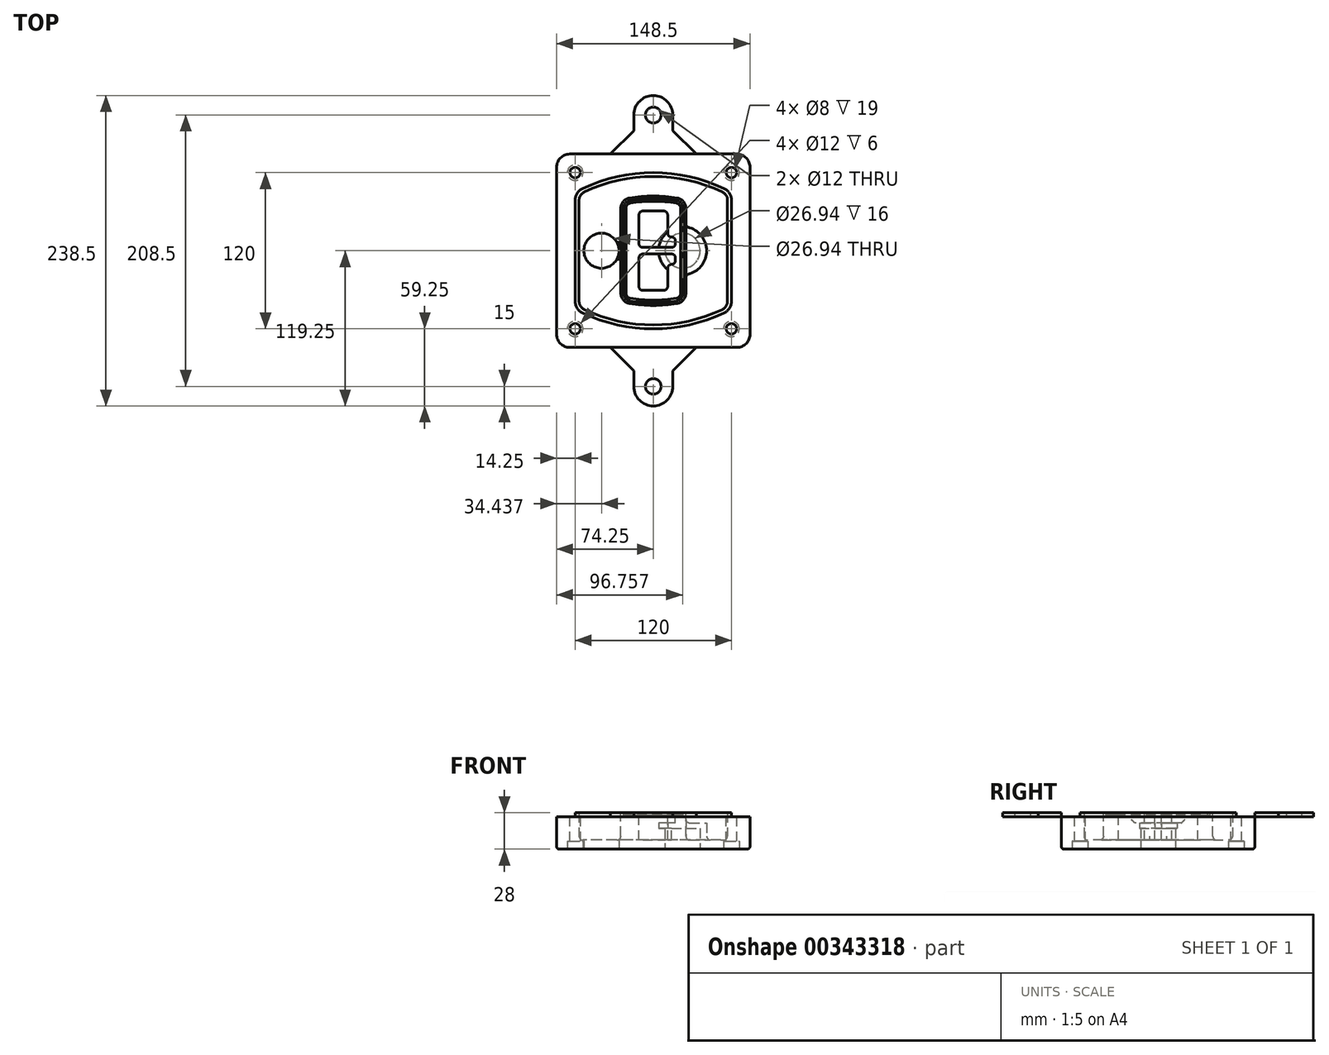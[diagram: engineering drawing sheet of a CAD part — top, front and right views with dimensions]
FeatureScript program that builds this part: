
annotation { "Feature Type Name" : "Feature", "Feature Type Description" : "" }
export const myFeature = defineFeature(function(context is Context, id is Id, definition is map)
    precondition{}
    {
        {
            var Q0;
            Q0=qCreatedBy(makeId("Top.planeOp"),FACE);
            var sketch = newSketch(context, id + "F0", { "sketchPlane" : qUnion([Q0])});
            skPoint(sketch, "E0.rect.middle", {"position": v(0, 0) * mm});
            skLineSegment(sketch, "E1.bottom", {"start": v(-64.25, -74.25) * mm, "end": v(64.25, -74.25) * mm});
            skLineSegment(sketch, "E1.top", {"start": v(-64.25, 74.25) * mm, "end": v(64.25, 74.25) * mm});
            skLineSegment(sketch, "E1.left", {"start": v(-74.25, -64.25) * mm, "end": v(-74.25, 64.25) * mm});
            skLineSegment(sketch, "E1.right", {"start": v(74.25, -64.25) * mm, "end": v(74.25, 64.25) * mm});
            skLineSegment(sketch, "E2", {"start": v(-74.25, 74.25) * mm, "end": v(74.25, -74.25) * mm, "construction": true});
            skLineSegment(sketch, "E3", {"start": v(74.25, 74.25) * mm, "end": v(-74.25, -74.25) * mm, "construction": true});
            skCircle(sketch, "E4", {"center": v(-60, 60) * mm, "radius": 4 * mm});
            skCircle(sketch, "E5", {"center": v(60, 60) * mm, "radius": 4 * mm});
            skCircle(sketch, "E6", {"center": v(60, -60) * mm, "radius": 4 * mm});
            skCircle(sketch, "E7", {"center": v(-60, -60) * mm, "radius": 4 * mm});
            skLineSegment(sketch, "E8", {"start": v(-60, 60) * mm, "end": v(60, 60) * mm, "construction": true});
            skLineSegment(sketch, "E9", {"start": v(60, 60) * mm, "end": v(60, -60) * mm, "construction": true});
            skLineSegment(sketch, "E10", {"start": v(60, -60) * mm, "end": v(-60, -60) * mm, "construction": true});
            skLineSegment(sketch, "E11", {"start": v(-60, -60) * mm, "end": v(-60, 60) * mm, "construction": true});
            skLineSegment(sketch, "E12", {"start": v(-60, 38.83) * mm, "end": v(-60, -38.83) * mm});
            skLineSegment(sketch, "E13", {"start": v(60, 38.83) * mm, "end": v(60, -38.83) * mm});
            skArc(sketch, "E14", {"start": v(54.26, 47.88) * mm, "mid": v(0, 60) * mm, "end": v(-54.26, 47.88) * mm});
            skArc(sketch, "E15", {"start": v(-54.26, -47.88) * mm, "mid": v(0, -60) * mm, "end": v(54.26, -47.88) * mm});
            skLineSegment(sketch, "E16", {"start": v(-60, 0) * mm, "end": v(60, 0) * mm, "construction": true});
            skPoint(sketch, "E17.visualSharp", {"position": v(-60, -45) * mm});
            skArc(sketch, "E17.filletArc", {"start": v(-60, -38.83) * mm, "mid": v(-58.44, -44.2) * mm, "end": v(-54.26, -47.88) * mm});
            skPoint(sketch, "E18.visualSharp", {"position": v(-60, 45) * mm});
            skArc(sketch, "E18.filletArc", {"start": v(-54.26, 47.88) * mm, "mid": v(-58.44, 44.2) * mm, "end": v(-60, 38.83) * mm});
            skPoint(sketch, "E19.visualSharp", {"position": v(60, 45) * mm});
            skArc(sketch, "E19.filletArc", {"start": v(60, 38.83) * mm, "mid": v(58.44, 44.2) * mm, "end": v(54.26, 47.88) * mm});
            skPoint(sketch, "E20.visualSharp", {"position": v(60, -45) * mm});
            skArc(sketch, "E20.filletArc", {"start": v(54.26, -47.88) * mm, "mid": v(58.44, -44.2) * mm, "end": v(60, -38.83) * mm});
            skPoint(sketch, "E21.visualSharp", {"position": v(-74.25, 74.25) * mm});
            skArc(sketch, "E21.filletArc", {"start": v(-64.25, 74.25) * mm, "mid": v(-71.32, 71.32) * mm, "end": v(-74.25, 64.25) * mm});
            skPoint(sketch, "E22.visualSharp", {"position": v(74.25, 74.25) * mm});
            skArc(sketch, "E22.filletArc", {"start": v(74.25, 64.25) * mm, "mid": v(71.32, 71.32) * mm, "end": v(64.25, 74.25) * mm});
            skPoint(sketch, "E23.visualSharp", {"position": v(74.25, -74.25) * mm});
            skArc(sketch, "E23.filletArc", {"start": v(64.25, -74.25) * mm, "mid": v(71.32, -71.32) * mm, "end": v(74.25, -64.25) * mm});
            skPoint(sketch, "E24.visualSharp", {"position": v(-74.25, -74.25) * mm});
            skArc(sketch, "E24.filletArc", {"start": v(-74.25, -64.25) * mm, "mid": v(-71.32, -71.32) * mm, "end": v(-64.25, -74.25) * mm});
            skArc(sketch, "E25.0", {"start": v(57, 38.83) * mm, "mid": v(55.9, 42.58) * mm, "end": v(52.98, 45.17) * mm});
            skLineSegment(sketch, "E25.1", {"start": v(57, 38.83) * mm, "end": v(57, -38.83) * mm});
            skArc(sketch, "E25.2", {"start": v(52.98, -45.17) * mm, "mid": v(55.9, -42.58) * mm, "end": v(57, -38.83) * mm});
            skArc(sketch, "E25.3", {"start": v(-52.98, -45.17) * mm, "mid": v(0, -57) * mm, "end": v(52.98, -45.17) * mm});
            skArc(sketch, "E25.4", {"start": v(-57, -38.83) * mm, "mid": v(-55.9, -42.58) * mm, "end": v(-52.98, -45.17) * mm});
            skArc(sketch, "E25.5", {"start": v(52.98, 45.17) * mm, "mid": v(0, 57) * mm, "end": v(-52.98, 45.17) * mm});
            skLineSegment(sketch, "E25.6", {"start": v(-57, 38.83) * mm, "end": v(-57, -38.83) * mm});
            skArc(sketch, "E25.7", {"start": v(-52.98, 45.17) * mm, "mid": v(-55.9, 42.58) * mm, "end": v(-57, 38.83) * mm});
            skArc(sketch, "E26.0", {"start": v(-55.96, 51.5) * mm, "mid": v(-61.82, 46.33) * mm, "end": v(-64, 38.83) * mm});
            skArc(sketch, "E26.1", {"start": v(55.96, 51.5) * mm, "mid": v(0, 64) * mm, "end": v(-55.96, 51.5) * mm});
            skArc(sketch, "E26.2", {"start": v(64, 38.83) * mm, "mid": v(61.82, 46.33) * mm, "end": v(55.96, 51.5) * mm});
            skLineSegment(sketch, "E26.3", {"start": v(64, 38.83) * mm, "end": v(64, -38.83) * mm});
            skArc(sketch, "E26.4", {"start": v(55.96, -51.5) * mm, "mid": v(61.82, -46.33) * mm, "end": v(64, -38.83) * mm});
            skLineSegment(sketch, "E26.5", {"start": v(-64, 38.83) * mm, "end": v(-64, -38.83) * mm});
            skArc(sketch, "E26.6", {"start": v(-55.96, -51.5) * mm, "mid": v(0, -64) * mm, "end": v(55.96, -51.5) * mm});
            skArc(sketch, "E26.7", {"start": v(-64, -38.83) * mm, "mid": v(-61.82, -46.33) * mm, "end": v(-55.96, -51.5) * mm});
            skSolve(sketch);
        }
        {
            var Q0;
            Q0=makeQuery(id+"F0.imprint","IMPRINT",FACE,{"disambiguationData":[TD([[makeQuery(id+"F0.imprint","IMPRINT",EDGE,{"derivedFrom":sQuery(id+"F0.wireOp",EDGE,"E1.bottom")}),1.0]])]});
            var Q1;
            Q1=makeQuery(id+"F0.imprint","IMPRINT",FACE,{"disambiguationData":[TD([[makeQuery(id+"F0.imprint","IMPRINT",EDGE,{"derivedFrom":sQuery(id+"F0.wireOp",EDGE,"E12")}),1.0]])]});
            var Q2;
            Q2=makeQuery(id+"F0.imprint","IMPRINT",FACE,{"disambiguationData":[TD([[makeQuery(id+"F0.imprint","IMPRINT",EDGE,{"derivedFrom":sQuery(id+"F0.wireOp",EDGE,"E25.0")}),1.0]])]});
            var Q3;
            Q3=makeQuery(id+"F0.imprint","IMPRINT",FACE,{"disambiguationData":[TD([[makeQuery(id+"F0.imprint","IMPRINT",EDGE,{"derivedFrom":sQuery(id+"F0.wireOp",EDGE,"E12")}),-1.0]])]});
            extrude(context, id + "F1", {"entities" : qUnion([Q0, Q1, Q2, Q3]), "oppositeDirection" : true, "depth" : 25 * mm});
        }
        {
            var Q0;
            Q0=makeQuery(id+"F0.imprint","IMPRINT",FACE,{"disambiguationData":[TD([[makeQuery(id+"F0.imprint","IMPRINT",EDGE,{"derivedFrom":sQuery(id+"F0.wireOp",EDGE,"E12")}),1.0]])]});
            extrude(context, id + "F2", {"entities" : qUnion([Q0]), "operationType" : NewBodyOperationType.ADD, "depth" : 3 * mm});
        }
        {
            var Q0;
            Q0=makeQuery(id+"F0.imprint","IMPRINT",FACE,{"disambiguationData":[TD([[makeQuery(id+"F0.imprint","IMPRINT",EDGE,{"derivedFrom":sQuery(id+"F0.wireOp",EDGE,"E25.0")}),1.0]])]});
            extrude(context, id + "F3", {"entities" : qUnion([Q0]), "operationType" : NewBodyOperationType.REMOVE, "oppositeDirection" : true, "depth" : 18 * mm});
        }
        {
            var Q0;
            Q0=makeQuery(id+"F2.opExtrude","CAP_FACE",FACE,{"disambiguationData":[OSD([sQuery(id+"F0.wireOp",EDGE,"E12"),sQuery(id+"F0.wireOp",EDGE,"E13"),sQuery(id+"F0.wireOp",EDGE,"E14"),sQuery(id+"F0.wireOp",EDGE,"E15"),sQuery(id+"F0.wireOp",EDGE,"E17.filletArc"),sQuery(id+"F0.wireOp",EDGE,"E18.filletArc"),sQuery(id+"F0.wireOp",EDGE,"E19.filletArc"),sQuery(id+"F0.wireOp",EDGE,"E20.filletArc"),sQuery(id+"F0.wireOp",EDGE,"E25.0"),sQuery(id+"F0.wireOp",EDGE,"E25.1"),sQuery(id+"F0.wireOp",EDGE,"E25.2"),sQuery(id+"F0.wireOp",EDGE,"E25.3"),sQuery(id+"F0.wireOp",EDGE,"E25.4"),sQuery(id+"F0.wireOp",EDGE,"E25.5"),sQuery(id+"F0.wireOp",EDGE,"E25.6"),sQuery(id+"F0.wireOp",EDGE,"E25.7")])],"isStart":false});
            var sketch = newSketch(context, id + "F4", { "sketchPlane" : qUnion([Q0])});
            skArc(sketch, "E27.0", {"start": v(-18.34, -40.45) * mm, "mid": v(0, -42) * mm, "end": v(18.34, -40.45) * mm});
            skArc(sketch, "E28.0", {"start": v(18.34, 40.45) * mm, "mid": v(0, 42) * mm, "end": v(-18.34, 40.45) * mm});
            skLineSegment(sketch, "E29", {"start": v(-25, 32.57) * mm, "end": v(-25, -32.57) * mm});
            skLineSegment(sketch, "E30", {"start": v(25, 32.57) * mm, "end": v(25, -32.57) * mm});
            skLineSegment(sketch, "E31", {"start": v(-25, 39.1) * mm, "end": v(25, 39.1) * mm, "construction": true});
            skLineSegment(sketch, "E32", {"start": v(-25, -39.1) * mm, "end": v(25, -39.1) * mm, "construction": true});
            skPoint(sketch, "E33.visualSharp", {"position": v(-25, 39.1) * mm});
            skArc(sketch, "E33.filletArc", {"start": v(-18.34, 40.45) * mm, "mid": v(-23.11, 37.73) * mm, "end": v(-25, 32.57) * mm});
            skPoint(sketch, "E34.visualSharp", {"position": v(25, 39.1) * mm});
            skArc(sketch, "E34.filletArc", {"start": v(25, 32.57) * mm, "mid": v(23.11, 37.73) * mm, "end": v(18.34, 40.45) * mm});
            skPoint(sketch, "E35.visualSharp", {"position": v(25, -39.1) * mm});
            skArc(sketch, "E35.filletArc", {"start": v(18.34, -40.45) * mm, "mid": v(23.11, -37.73) * mm, "end": v(25, -32.57) * mm});
            skPoint(sketch, "E36.visualSharp", {"position": v(-25, -39.1) * mm});
            skArc(sketch, "E36.filletArc", {"start": v(-25, -32.57) * mm, "mid": v(-23.11, -37.73) * mm, "end": v(-18.34, -40.45) * mm});
            skArc(sketch, "E37.0", {"start": v(52.98, 45.17) * mm, "mid": v(0, 57) * mm, "end": v(-52.98, 45.17) * mm});
            skArc(sketch, "E37.1", {"start": v(-52.98, 45.17) * mm, "mid": v(-55.9, 42.58) * mm, "end": v(-57, 38.83) * mm});
            skLineSegment(sketch, "E37.2", {"start": v(-57, 38.83) * mm, "end": v(-57, -38.83) * mm});
            skArc(sketch, "E37.3", {"start": v(-57, -38.83) * mm, "mid": v(-55.9, -42.58) * mm, "end": v(-52.98, -45.17) * mm});
            skArc(sketch, "E37.4", {"start": v(-52.98, -45.17) * mm, "mid": v(0, -57) * mm, "end": v(52.98, -45.17) * mm});
            skArc(sketch, "E37.5", {"start": v(52.98, -45.17) * mm, "mid": v(55.9, -42.58) * mm, "end": v(57, -38.83) * mm});
            skLineSegment(sketch, "E37.6", {"start": v(57, 38.83) * mm, "end": v(57, -38.83) * mm});
            skArc(sketch, "E37.7", {"start": v(57, 38.83) * mm, "mid": v(55.9, 42.58) * mm, "end": v(52.98, 45.17) * mm});
            skLineSegment(sketch, "E38.0", {"start": v(23, 32.57) * mm, "end": v(23, -32.57) * mm});
            skArc(sketch, "E38.1", {"start": v(18, -38.48) * mm, "mid": v(21.58, -36.44) * mm, "end": v(23, -32.57) * mm});
            skArc(sketch, "E38.2", {"start": v(-18, -38.48) * mm, "mid": v(0, -40) * mm, "end": v(18, -38.48) * mm});
            skArc(sketch, "E38.3", {"start": v(-23, -32.57) * mm, "mid": v(-21.58, -36.44) * mm, "end": v(-18, -38.48) * mm});
            skLineSegment(sketch, "E38.4", {"start": v(-23, 32.57) * mm, "end": v(-23, -32.57) * mm});
            skArc(sketch, "E38.5", {"start": v(23, 32.57) * mm, "mid": v(21.58, 36.44) * mm, "end": v(18, 38.48) * mm});
            skArc(sketch, "E38.6", {"start": v(-18, 38.48) * mm, "mid": v(-21.58, 36.44) * mm, "end": v(-23, 32.57) * mm});
            skArc(sketch, "E38.7", {"start": v(18, 38.48) * mm, "mid": v(0, 40) * mm, "end": v(-18, 38.48) * mm});
            skArc(sketch, "E39.0", {"start": v(21, 32.57) * mm, "mid": v(20.06, 35.15) * mm, "end": v(17.67, 36.5) * mm});
            skLineSegment(sketch, "E39.1", {"start": v(21, 32.57) * mm, "end": v(21, -32.57) * mm});
            skArc(sketch, "E39.2", {"start": v(17.67, -36.5) * mm, "mid": v(20.06, -35.15) * mm, "end": v(21, -32.57) * mm});
            skArc(sketch, "E39.3", {"start": v(-17.67, -36.5) * mm, "mid": v(0, -38) * mm, "end": v(17.67, -36.5) * mm});
            skArc(sketch, "E39.4", {"start": v(-21, -32.57) * mm, "mid": v(-20.06, -35.15) * mm, "end": v(-17.67, -36.5) * mm});
            skArc(sketch, "E39.5", {"start": v(17.67, 36.5) * mm, "mid": v(0, 38) * mm, "end": v(-17.67, 36.5) * mm});
            skLineSegment(sketch, "E39.6", {"start": v(-21, 32.57) * mm, "end": v(-21, -32.57) * mm});
            skArc(sketch, "E39.7", {"start": v(-17.67, 36.5) * mm, "mid": v(-20.06, 35.15) * mm, "end": v(-21, 32.57) * mm});
            skLineSegment(sketch, "E40", {"start": v(-25, 0) * mm, "end": v(25, 0) * mm, "construction": true});
            skLineSegment(sketch, "E41", {"start": v(-11, 5.5) * mm, "end": v(-11, 27.5) * mm});
            skLineSegment(sketch, "E42", {"start": v(-8, 30.5) * mm, "end": v(8, 30.5) * mm});
            skLineSegment(sketch, "E43", {"start": v(11, 27.5) * mm, "end": v(11, 13.5) * mm});
            skLineSegment(sketch, "E44", {"start": v(14, 10.5) * mm, "end": v(14, 10.5) * mm});
            skLineSegment(sketch, "E45", {"start": v(17, 7.5) * mm, "end": v(17, 5.5) * mm});
            skLineSegment(sketch, "E46", {"start": v(14, 2.5) * mm, "end": v(-8, 2.5) * mm});
            skPoint(sketch, "E47.visualSharp", {"position": v(-11, 30.5) * mm});
            skArc(sketch, "E47.filletArc", {"start": v(-8, 30.5) * mm, "mid": v(-10.12, 29.62) * mm, "end": v(-11, 27.5) * mm});
            skPoint(sketch, "E48.visualSharp", {"position": v(11, 30.5) * mm});
            skArc(sketch, "E48.filletArc", {"start": v(11, 27.5) * mm, "mid": v(10.12, 29.62) * mm, "end": v(8, 30.5) * mm});
            skPoint(sketch, "E49.visualSharp", {"position": v(11, 10.5) * mm});
            skArc(sketch, "E49.filletArc", {"start": v(11, 13.5) * mm, "mid": v(11.88, 11.38) * mm, "end": v(14, 10.5) * mm});
            skPoint(sketch, "E50.visualSharp", {"position": v(17, 10.5) * mm});
            skArc(sketch, "E50.filletArc", {"start": v(17, 7.5) * mm, "mid": v(16.12, 9.62) * mm, "end": v(14, 10.5) * mm});
            skPoint(sketch, "E51.visualSharp", {"position": v(17, 2.5) * mm});
            skArc(sketch, "E51.filletArc", {"start": v(14, 2.5) * mm, "mid": v(16.12, 3.38) * mm, "end": v(17, 5.5) * mm});
            skPoint(sketch, "E52.visualSharp", {"position": v(-11, 2.5) * mm});
            skArc(sketch, "E52.filletArc", {"start": v(-11, 5.5) * mm, "mid": v(-10.12, 3.38) * mm, "end": v(-8, 2.5) * mm});
            skLineSegment(sketch, "E53.0.MirrorCS", {"start": v(14, -2.5) * mm, "end": v(-8, -2.5) * mm});
            skArc(sketch, "E54.0.MirrorCS", {"start": v(-11, -5.5) * mm, "mid": v(-10.12, -3.38) * mm, "end": v(-8, -2.5) * mm});
            skLineSegment(sketch, "E55.0.MirrorCS", {"start": v(-11, -5.5) * mm, "end": v(-11, -27.5) * mm});
            skArc(sketch, "E56.0.MirrorCS", {"start": v(-8, -30.5) * mm, "mid": v(-10.12, -29.62) * mm, "end": v(-11, -27.5) * mm});
            skLineSegment(sketch, "E57.0.MirrorCS", {"start": v(-8, -30.5) * mm, "end": v(8, -30.5) * mm});
            skArc(sketch, "E58.0.MirrorCS", {"start": v(11, -27.5) * mm, "mid": v(10.12, -29.62) * mm, "end": v(8, -30.5) * mm});
            skLineSegment(sketch, "E59.0.MirrorCS", {"start": v(11, -27.5) * mm, "end": v(11, -13.5) * mm});
            skArc(sketch, "E60.0.MirrorCS", {"start": v(11, -13.5) * mm, "mid": v(11.88, -11.38) * mm, "end": v(14, -10.5) * mm});
            skArc(sketch, "E61.0.MirrorCS", {"start": v(17, -7.5) * mm, "mid": v(16.12, -9.62) * mm, "end": v(14, -10.5) * mm});
            skLineSegment(sketch, "E62.0.MirrorCS", {"start": v(17, -7.5) * mm, "end": v(17, -5.5) * mm});
            skArc(sketch, "E63.0.MirrorCS", {"start": v(14, -2.5) * mm, "mid": v(16.12, -3.38) * mm, "end": v(17, -5.5) * mm});
            skSolve(sketch);
        }
        {
            var Q0;
            Q0=makeQuery(id+"F4.imprint","IMPRINT",FACE,{"disambiguationData":[TD([[makeQuery(id+"F4.imprint","IMPRINT",EDGE,{"derivedFrom":sQuery(id+"F4.wireOp",EDGE,"E27.0")}),1.0]])]});
            var Q1;
            Q1=makeQuery(id+"F4.imprint","IMPRINT",FACE,{"disambiguationData":[TD([[makeQuery(id+"F4.imprint","IMPRINT",EDGE,{"derivedFrom":sQuery(id+"F4.wireOp",EDGE,"E38.0")}),-1.0]])]});
            var Q2;
            Q2=makeQuery(id+"F4.imprint","IMPRINT",FACE,{"disambiguationData":[TD([[makeQuery(id+"F4.imprint","IMPRINT",EDGE,{"derivedFrom":sQuery(id+"F4.wireOp",EDGE,"E39.0")}),1.0]])]});
            extrude(context, id + "F5", {"entities" : qUnion([Q0, Q1, Q2]), "operationType" : NewBodyOperationType.ADD, "endBound" : BoundingType.UP_TO_NEXT, "oppositeDirection" : true, "depth" : 25 * mm});
        }
        {
            var Q0;
            Q0=makeQuery(id+"F4.imprint","IMPRINT",FACE,{"disambiguationData":[TD([[makeQuery(id+"F4.imprint","IMPRINT",EDGE,{"derivedFrom":sQuery(id+"F4.wireOp",EDGE,"E38.0")}),-1.0]])]});
            extrude(context, id + "F6", {"entities" : qUnion([Q0]), "operationType" : NewBodyOperationType.REMOVE, "oppositeDirection" : true, "depth" : 2 * mm});
        }
        {
            var Q0;
            Q0=makeQuery(id+"F1.opExtrude","CAP_FACE",FACE,{"disambiguationData":[OSD([sQuery(id+"F0.wireOp",EDGE,"E1.bottom"),sQuery(id+"F0.wireOp",EDGE,"E1.top"),sQuery(id+"F0.wireOp",EDGE,"E1.left"),sQuery(id+"F0.wireOp",EDGE,"E1.right"),sQuery(id+"F0.wireOp",EDGE,"E4"),sQuery(id+"F0.wireOp",EDGE,"E5"),sQuery(id+"F0.wireOp",EDGE,"E6"),sQuery(id+"F0.wireOp",EDGE,"E7"),sQuery(id+"F0.wireOp",EDGE,"E21.filletArc"),sQuery(id+"F0.wireOp",EDGE,"E22.filletArc"),sQuery(id+"F0.wireOp",EDGE,"E23.filletArc"),sQuery(id+"F0.wireOp",EDGE,"E24.filletArc")])],"isStart":false});
            var sketch = newSketch(context, id + "F7", { "sketchPlane" : qUnion([Q0])});
            skCircle(sketch, "E64", {"center": v(22.5, 0) * mm, "radius": 13.47 * mm});
            skCircle(sketch, "E65", {"center": v(-39.81, 0) * mm, "radius": 13.47 * mm});
            skLineSegment(sketch, "E66", {"start": v(74.25, 0) * mm, "end": v(-74.25, 0) * mm});
            skCircle(sketch, "E67", {"center": v(22.5, 0) * mm, "radius": 18.47 * mm});
            skCircle(sketch, "E68", {"center": v(60, -60) * mm, "radius": 6 * mm});
            skCircle(sketch, "E69", {"center": v(-60, -60) * mm, "radius": 6 * mm});
            skCircle(sketch, "E70", {"center": v(-60, 60) * mm, "radius": 6 * mm});
            skCircle(sketch, "E71", {"center": v(60, 60) * mm, "radius": 6 * mm});
            skSolve(sketch);
        }
        {
            var Q0;
            {var subQ1=sQuery(id+"F7.wireOp",EDGE,"E66");var subQ4=sQuery(id+"F7.wireOp",EDGE,"E64");var subQ6=makeQuery(id+"F7.imprint","INTERSECT",VERTEX,{"disambiguationData":[OD(0.0)],"derivedFrom":[subQ4,subQ1]});Q0=makeQuery(id+"F7.imprint","IMPRINT",FACE,{"disambiguationData":[TD([[makeQuery(id+"F7.imprint","IMPRINT",EDGE,{"disambiguationData":[TD([[subQ6,-1.0]])],"derivedFrom":subQ4}),-1.0]])]});}
            var Q1;
            {var subQ0=sQuery(id+"F7.wireOp",EDGE,"E66");var subQ1=sQuery(id+"F7.wireOp",EDGE,"E64");var subQ3=makeQuery(id+"F7.imprint","INTERSECT",VERTEX,{"disambiguationData":[OD(0.0)],"derivedFrom":[subQ1,subQ0]});Q1=makeQuery(id+"F7.imprint","IMPRINT",FACE,{"disambiguationData":[TD([[makeQuery(id+"F7.imprint","IMPRINT",EDGE,{"disambiguationData":[TD([[subQ3,-1.0]])],"derivedFrom":subQ1}),1.0]])]});}
            var Q2;
            {var subQ0=sQuery(id+"F7.wireOp",EDGE,"E66");var subQ1=sQuery(id+"F7.wireOp",EDGE,"E64");var subQ3=makeQuery(id+"F7.imprint","INTERSECT",VERTEX,{"disambiguationData":[OD(0.0)],"derivedFrom":[subQ1,subQ0]});Q2=makeQuery(id+"F7.imprint","IMPRINT",FACE,{"disambiguationData":[TD([[makeQuery(id+"F7.imprint","IMPRINT",EDGE,{"disambiguationData":[TD([[subQ3,1.0]])],"derivedFrom":subQ1}),1.0]])]});}
            var Q3;
            {var subQ1=sQuery(id+"F7.wireOp",EDGE,"E66");var subQ4=sQuery(id+"F7.wireOp",EDGE,"E64");var subQ6=makeQuery(id+"F7.imprint","INTERSECT",VERTEX,{"disambiguationData":[OD(0.0)],"derivedFrom":[subQ4,subQ1]});Q3=makeQuery(id+"F7.imprint","IMPRINT",FACE,{"disambiguationData":[TD([[makeQuery(id+"F7.imprint","IMPRINT",EDGE,{"disambiguationData":[TD([[subQ6,1.0]])],"derivedFrom":subQ4}),-1.0]])]});}
            extrude(context, id + "F8", {"entities" : qUnion([Q0, Q1, Q2, Q3]), "operationType" : NewBodyOperationType.ADD, "oppositeDirection" : true, "depth" : 20 * mm});
        }
        {
            var Q0;
            {var subQ0=sQuery(id+"F7.wireOp",EDGE,"E66");var subQ1=sQuery(id+"F7.wireOp",EDGE,"E64");var subQ3=makeQuery(id+"F7.imprint","INTERSECT",VERTEX,{"disambiguationData":[OD(0.0)],"derivedFrom":[subQ1,subQ0]});Q0=makeQuery(id+"F7.imprint","IMPRINT",FACE,{"disambiguationData":[TD([[makeQuery(id+"F7.imprint","IMPRINT",EDGE,{"disambiguationData":[TD([[subQ3,-1.0]])],"derivedFrom":subQ1}),1.0]])]});}
            var Q1;
            {var subQ0=sQuery(id+"F7.wireOp",EDGE,"E66");var subQ1=sQuery(id+"F7.wireOp",EDGE,"E64");var subQ3=makeQuery(id+"F7.imprint","INTERSECT",VERTEX,{"disambiguationData":[OD(0.0)],"derivedFrom":[subQ1,subQ0]});Q1=makeQuery(id+"F7.imprint","IMPRINT",FACE,{"disambiguationData":[TD([[makeQuery(id+"F7.imprint","IMPRINT",EDGE,{"disambiguationData":[TD([[subQ3,1.0]])],"derivedFrom":subQ1}),1.0]])]});}
            extrude(context, id + "F9", {"entities" : qUnion([Q0, Q1]), "operationType" : NewBodyOperationType.REMOVE, "oppositeDirection" : true, "depth" : 16 * mm});
        }
        {
            var Q0;
            {var subQ0=sQuery(id+"F7.wireOp",EDGE,"E66");var subQ1=sQuery(id+"F7.wireOp",EDGE,"E65");var subQ3=makeQuery(id+"F7.imprint","INTERSECT",VERTEX,{"disambiguationData":[OD(0.0)],"derivedFrom":[subQ1,subQ0]});Q0=makeQuery(id+"F7.imprint","IMPRINT",FACE,{"disambiguationData":[TD([[makeQuery(id+"F7.imprint","IMPRINT",EDGE,{"disambiguationData":[TD([[subQ3,-1.0]])],"derivedFrom":subQ1}),1.0]])]});}
            var Q1;
            {var subQ0=sQuery(id+"F7.wireOp",EDGE,"E66");var subQ1=sQuery(id+"F7.wireOp",EDGE,"E65");var subQ3=makeQuery(id+"F7.imprint","INTERSECT",VERTEX,{"disambiguationData":[OD(0.0)],"derivedFrom":[subQ1,subQ0]});Q1=makeQuery(id+"F7.imprint","IMPRINT",FACE,{"disambiguationData":[TD([[makeQuery(id+"F7.imprint","IMPRINT",EDGE,{"disambiguationData":[TD([[subQ3,1.0]])],"derivedFrom":subQ1}),1.0]])]});}
            extrude(context, id + "F10", {"entities" : qUnion([Q0, Q1]), "operationType" : NewBodyOperationType.REMOVE, "oppositeDirection" : true, "depth" : 25 * mm});
        }
        {
            var Q0;
            Q0=makeQuery(id+"F7.imprint","IMPRINT",FACE,{"disambiguationData":[TD([[makeQuery(id+"F7.imprint","IMPRINT",EDGE,{"derivedFrom":sQuery(id+"F7.wireOp",EDGE,"E68")}),1.0]])]});
            var Q1;
            Q1=makeQuery(id+"F7.imprint","IMPRINT",FACE,{"disambiguationData":[TD([[makeQuery(id+"F7.imprint","IMPRINT",EDGE,{"derivedFrom":makeQuery(id+"F1.opExtrude","CAP_EDGE",EDGE,{"disambiguationData":[OSD([sQuery(id+"F0.wireOp",EDGE,"E5")])],"isStart":false})}),-1.0]])]});
            var Q2;
            Q2=makeQuery(id+"F7.imprint","IMPRINT",FACE,{"disambiguationData":[TD([[makeQuery(id+"F7.imprint","IMPRINT",EDGE,{"derivedFrom":sQuery(id+"F7.wireOp",EDGE,"E69")}),1.0]])]});
            var Q3;
            Q3=makeQuery(id+"F7.imprint","IMPRINT",FACE,{"disambiguationData":[TD([[makeQuery(id+"F7.imprint","IMPRINT",EDGE,{"derivedFrom":makeQuery(id+"F1.opExtrude","CAP_EDGE",EDGE,{"disambiguationData":[OSD([sQuery(id+"F0.wireOp",EDGE,"E4")])],"isStart":false})}),-1.0]])]});
            var Q4;
            Q4=makeQuery(id+"F7.imprint","IMPRINT",FACE,{"disambiguationData":[TD([[makeQuery(id+"F7.imprint","IMPRINT",EDGE,{"derivedFrom":sQuery(id+"F7.wireOp",EDGE,"E70")}),1.0]])]});
            var Q5;
            Q5=makeQuery(id+"F7.imprint","IMPRINT",FACE,{"disambiguationData":[TD([[makeQuery(id+"F7.imprint","IMPRINT",EDGE,{"derivedFrom":makeQuery(id+"F1.opExtrude","CAP_EDGE",EDGE,{"disambiguationData":[OSD([sQuery(id+"F0.wireOp",EDGE,"E7")])],"isStart":false})}),-1.0]])]});
            var Q6;
            Q6=makeQuery(id+"F7.imprint","IMPRINT",FACE,{"disambiguationData":[TD([[makeQuery(id+"F7.imprint","IMPRINT",EDGE,{"derivedFrom":sQuery(id+"F7.wireOp",EDGE,"E71")}),1.0]])]});
            var Q7;
            Q7=makeQuery(id+"F7.imprint","IMPRINT",FACE,{"disambiguationData":[TD([[makeQuery(id+"F7.imprint","IMPRINT",EDGE,{"derivedFrom":makeQuery(id+"F1.opExtrude","CAP_EDGE",EDGE,{"disambiguationData":[OSD([sQuery(id+"F0.wireOp",EDGE,"E6")])],"isStart":false})}),-1.0]])]});
            extrude(context, id + "F11", {"entities" : qUnion([Q0, Q1, Q2, Q3, Q4, Q5, Q6, Q7]), "operationType" : NewBodyOperationType.REMOVE, "oppositeDirection" : true, "depth" : 6 * mm});
        }
        {
            var Q0;
            Q0=makeQuery(id+"F9.boolean.opBoolean","COPY",FACE,{"derivedFrom":makeQuery(id+"F9.opExtrude","CAP_FACE",FACE,{"disambiguationData":[OSD([sQuery(id+"F7.wireOp",EDGE,"E64")])],"isStart":false})});
            var sketch = newSketch(context, id + "F12", { "sketchPlane" : qUnion([Q0])});
            skArc(sketch, "E72.0", {"start": v(11, 14.45) * mm, "mid": v(6.45, 9.13) * mm, "end": v(4.2, 2.5) * mm});
            skArc(sketch, "E72.1", {"start": v(4.2, -2.5) * mm, "mid": v(6.45, -9.13) * mm, "end": v(11, -14.45) * mm});
            skLineSegment(sketch, "E73", {"start": v(4.2, -2.5) * mm, "end": v(14, -2.5) * mm});
            skLineSegment(sketch, "E74.0", {"start": v(14, 2.5) * mm, "end": v(4.2, 2.5) * mm});
            skArc(sketch, "E74.1", {"start": v(14, 2.5) * mm, "mid": v(16.12, 3.38) * mm, "end": v(17, 5.5) * mm});
            skLineSegment(sketch, "E74.2", {"start": v(17, 7.5) * mm, "end": v(17, 5.5) * mm});
            skArc(sketch, "E74.3", {"start": v(17, 7.5) * mm, "mid": v(16.12, 9.62) * mm, "end": v(14, 10.5) * mm});
            skArc(sketch, "E74.4", {"start": v(11, 13.5) * mm, "mid": v(11.88, 11.38) * mm, "end": v(14, 10.5) * mm});
            skLineSegment(sketch, "E74.5", {"start": v(11, 14.45) * mm, "end": v(11, 13.5) * mm});
            skLineSegment(sketch, "E74.7", {"start": v(14, -2.5) * mm, "end": v(4.2, -2.5) * mm});
            skArc(sketch, "E74.8", {"start": v(14, -2.5) * mm, "mid": v(16.12, -3.38) * mm, "end": v(17, -5.5) * mm});
            skLineSegment(sketch, "E74.9", {"start": v(17, -7.5) * mm, "end": v(17, -5.5) * mm});
            skArc(sketch, "E74.10", {"start": v(17, -7.5) * mm, "mid": v(16.12, -9.62) * mm, "end": v(14, -10.5) * mm});
            skArc(sketch, "E74.11", {"start": v(11, -13.5) * mm, "mid": v(11.88, -11.38) * mm, "end": v(14, -10.5) * mm});
            skLineSegment(sketch, "E74.12", {"start": v(11, -14.45) * mm, "end": v(11, -13.5) * mm});
            skPoint(sketch, "E75.orphan", {"position": v(11, -27.5) * mm});
            skPoint(sketch, "E76.orphan", {"position": v(-8, -2.5) * mm});
            skPoint(sketch, "E77.orphan", {"position": v(-8, 2.5) * mm});
            skPoint(sketch, "E78.orphan", {"position": v(11, 27.5) * mm});
            skSolve(sketch);
        }
        {
            var Q0;
            {var subQ7=sQuery(id+"F12.wireOp",EDGE,"E72.0");var subQ14=sQuery(id+"F12.wireOp",EDGE,"E72.1");var subQ16=sQuery(id+"F12.wireOp",EDGE,"E74.1");var subQ18=sQuery(id+"F12.wireOp",EDGE,"E74.8");Q0=qUnion([makeQuery(id+"F12.imprint","IMPRINT",FACE,{"disambiguationData":[TD([[makeQuery(id+"F12.imprint","IMPRINT",EDGE,{"derivedFrom":subQ7}),1.0]])]}),makeQuery(id+"F12.imprint","IMPRINT",FACE,{"disambiguationData":[TD([[makeQuery(id+"F12.imprint","IMPRINT",EDGE,{"derivedFrom":subQ14}),1.0]])]}),makeQuery(id+"F12.imprint","IMPRINT",FACE,{"disambiguationData":[TD([[makeQuery(id+"F12.imprint","IMPRINT",EDGE,{"derivedFrom":subQ16}),1.0]])]}),makeQuery(id+"F12.imprint","IMPRINT",FACE,{"disambiguationData":[TD([[makeQuery(id+"F12.imprint","IMPRINT",EDGE,{"derivedFrom":subQ18}),-1.0]])]})]);}
            var Q1;
            Q1=makeQuery(id+"F5.boolean.opBoolean","SPLIT",FACE,{"disambiguationData":[TD([makeQuery(id+"F5.opExtrude","SWEPT_FACE",FACE,{"disambiguationData":[OSD([sQuery(id+"F4.wireOp",EDGE,"E41")])]})])],"derivedFrom":makeQuery(id+"F3.boolean.opBoolean","COPY",FACE,{"derivedFrom":makeQuery(id+"F3.opExtrude","CAP_FACE",FACE,{"disambiguationData":[OSD([sQuery(id+"F0.wireOp",EDGE,"E25.0"),sQuery(id+"F0.wireOp",EDGE,"E25.1"),sQuery(id+"F0.wireOp",EDGE,"E25.2"),sQuery(id+"F0.wireOp",EDGE,"E25.3"),sQuery(id+"F0.wireOp",EDGE,"E25.4"),sQuery(id+"F0.wireOp",EDGE,"E25.5"),sQuery(id+"F0.wireOp",EDGE,"E25.6"),sQuery(id+"F0.wireOp",EDGE,"E25.7")])],"isStart":false})})});
            extrude(context, id + "F13", {"entities" : qUnion([Q0]), "operationType" : NewBodyOperationType.REMOVE, "endBound" : BoundingType.UP_TO_SURFACE, "endBoundEntityFace" : qUnion([Q1]), "depth" : 25 * mm});
        }
        {
            var Q0;
            Q0=makeQuery(id+"F3.boolean.opBoolean","COPY",EDGE,{"derivedFrom":makeQuery(id+"F3.opExtrude","CAP_EDGE",EDGE,{"disambiguationData":[OSD([sQuery(id+"F0.wireOp",EDGE,"E25.6")])],"isStart":false})});
            var Q1;
            Q1=makeQuery(id+"F8.boolean.opBoolean","INTERSECT",EDGE,{"derivedFrom":[makeQuery(id+"F5.opExtrude","SWEPT_FACE",FACE,{"disambiguationData":[OSD([sQuery(id+"F4.wireOp",EDGE,"E30")])]}),makeQuery(id+"F8.opExtrude","CAP_FACE",FACE,{"disambiguationData":[OSD([sQuery(id+"F7.wireOp",EDGE,"E67")])],"isStart":false})]});
            var Q2;
            Q2=makeQuery(id+"F8.boolean.opBoolean","INTERSECT",EDGE,{"disambiguationData":[OD(1.0)],"derivedFrom":[makeQuery(id+"F5.opExtrude","SWEPT_FACE",FACE,{"disambiguationData":[OSD([sQuery(id+"F4.wireOp",EDGE,"E30")])]}),makeQuery(id+"F8.opExtrude","SWEPT_FACE",FACE,{"disambiguationData":[OSD([sQuery(id+"F7.wireOp",EDGE,"E67")])]})]});
            var Q3;
            {var subQ0=sQuery(id+"F4.wireOp",EDGE,"E30");Q3=makeQuery(id+"F8.boolean.opBoolean","SPLIT",EDGE,{"disambiguationData":[TD([makeQuery(id+"F5.opExtrude","SWEPT_FACE",FACE,{"disambiguationData":[OSD([sQuery(id+"F4.wireOp",EDGE,"E35.filletArc")])]})])],"derivedFrom":makeQuery(id+"F5.opExtrude","CAP_EDGE",EDGE,{"disambiguationData":[OSD([subQ0])],"isStart":false})});}
            var Q4;
            {var subQ0=sQuery(id+"F0.wireOp",EDGE,"E25.7");var subQ1=sQuery(id+"F0.wireOp",EDGE,"E25.1");var subQ2=sQuery(id+"F0.wireOp",EDGE,"E25.6");var subQ3=sQuery(id+"F0.wireOp",EDGE,"E25.5");var subQ4=sQuery(id+"F0.wireOp",EDGE,"E25.4");var subQ5=sQuery(id+"F0.wireOp",EDGE,"E25.0");var subQ6=sQuery(id+"F0.wireOp",EDGE,"E25.2");var subQ7=sQuery(id+"F0.wireOp",EDGE,"E25.3");Q4=makeQuery(id+"F8.boolean.opBoolean","INTERSECT",EDGE,{"derivedFrom":[makeQuery(id+"F5.boolean.opBoolean","SPLIT",FACE,{"disambiguationData":[TD([makeQuery(id+"F2.opExtrude","SWEPT_FACE",FACE,{"disambiguationData":[OSD([subQ5])]})])],"derivedFrom":makeQuery(id+"F3.boolean.opBoolean","COPY",FACE,{"derivedFrom":makeQuery(id+"F3.opExtrude","CAP_FACE",FACE,{"disambiguationData":[OSD([subQ5,subQ1,subQ6,subQ7,subQ4,subQ3,subQ2,subQ0])],"isStart":false})})}),makeQuery(id+"F8.opExtrude","SWEPT_FACE",FACE,{"disambiguationData":[OSD([sQuery(id+"F7.wireOp",EDGE,"E67")])]})]});}
            var Q5;
            Q5=makeQuery(id+"F8.boolean.opBoolean","INTERSECT",EDGE,{"disambiguationData":[OD(0.0)],"derivedFrom":[makeQuery(id+"F5.opExtrude","SWEPT_FACE",FACE,{"disambiguationData":[OSD([sQuery(id+"F4.wireOp",EDGE,"E30")])]}),makeQuery(id+"F8.opExtrude","SWEPT_FACE",FACE,{"disambiguationData":[OSD([sQuery(id+"F7.wireOp",EDGE,"E67")])]})]});
            fillet(context, id + "F14", {"entities" : qUnion([Q0, Q1, Q2, Q3, Q4, Q5]), "radius" : 3 * mm, "tangentPropagation" : true, "allowEdgeOverflow" : false});
        }
        {
            var Q0;
            Q0=makeQuery(id+"F1.opExtrude","CAP_EDGE",EDGE,{"disambiguationData":[OSD([sQuery(id+"F0.wireOp",EDGE,"E1.bottom")])],"isStart":false});
            fillet(context, id + "F15", {"entities" : qUnion([Q0]), "radius" : 2 * mm, "tangentPropagation" : true, "allowEdgeOverflow" : false});
        }
        {
            var Q0;
            {var subQ0=sQuery(id+"F0.wireOp",EDGE,"E21.filletArc");var subQ1=sQuery(id+"F0.wireOp",EDGE,"E7");var subQ2=sQuery(id+"F0.wireOp",EDGE,"E6");var subQ3=sQuery(id+"F0.wireOp",EDGE,"E5");var subQ4=sQuery(id+"F0.wireOp",EDGE,"E4");var subQ5=sQuery(id+"F0.wireOp",EDGE,"E22.filletArc");var subQ6=sQuery(id+"F0.wireOp",EDGE,"E1.bottom");var subQ7=sQuery(id+"F0.wireOp",EDGE,"E1.right");var subQ8=sQuery(id+"F0.wireOp",EDGE,"E1.top");var subQ9=sQuery(id+"F0.wireOp",EDGE,"E1.left");var subQ10=sQuery(id+"F0.wireOp",EDGE,"E23.filletArc");var subQ11=sQuery(id+"F0.wireOp",EDGE,"E24.filletArc");Q0=makeQuery(id+"F2.boolean.opBoolean","SPLIT",FACE,{"disambiguationData":[TD([makeQuery(id+"F1.opExtrude","SWEPT_FACE",FACE,{"disambiguationData":[OSD([subQ6])]})])],"derivedFrom":makeQuery(id+"F1.opExtrude","CAP_FACE",FACE,{"disambiguationData":[OSD([subQ6,subQ8,subQ9,subQ7,subQ4,subQ3,subQ2,subQ1,subQ0,subQ5,subQ10,subQ11])],"isStart":true})});}
            var sketch = newSketch(context, id + "F16", { "sketchPlane" : qUnion([Q0])});
            skLineSegment(sketch, "E79", {"start": v(0, 74.25) * mm, "end": v(0, 104.25) * mm, "construction": true});
            skLineSegment(sketch, "E80", {"start": v(-33, 74.25) * mm, "end": v(-15, 92.25) * mm});
            skLineSegment(sketch, "E81", {"start": v(15, 92.25) * mm, "end": v(33, 74.25) * mm});
            skCircle(sketch, "E82", {"center": v(0, 104.25) * mm, "radius": 6 * mm});
            skLineSegment(sketch, "E83", {"start": v(-15, 92.25) * mm, "end": v(-15, 104.25) * mm});
            skLineSegment(sketch, "E84", {"start": v(15, 92.25) * mm, "end": v(15, 104.25) * mm});
            skArc(sketch, "E85", {"start": v(15, 104.25) * mm, "mid": v(0, 119.25) * mm, "end": v(-15, 104.25) * mm});
            skLineSegment(sketch, "E86", {"start": v(0, 0) * mm, "end": v(-74.25, 0) * mm, "construction": true});
            skLineSegment(sketch, "E87", {"start": v(0, 0) * mm, "end": v(74.25, 0) * mm, "construction": true});
            skLineSegment(sketch, "E88.MirrorCS", {"start": v(-33, -74.25) * mm, "end": v(-15, -92.25) * mm});
            skLineSegment(sketch, "E89.MirrorCS", {"start": v(-15, -92.25) * mm, "end": v(-15, -104.25) * mm});
            skArc(sketch, "E90.MirrorCS", {"start": v(15, -104.25) * mm, "mid": v(0, -119.25) * mm, "end": v(-15, -104.25) * mm});
            skLineSegment(sketch, "E91.MirrorCS", {"start": v(15, -92.25) * mm, "end": v(15, -104.25) * mm});
            skLineSegment(sketch, "E92.MirrorCS", {"start": v(15, -92.25) * mm, "end": v(33, -74.25) * mm});
            skCircle(sketch, "E93.MirrorC", {"center": v(0, -104.25) * mm, "radius": 6 * mm});
            skLineSegment(sketch, "E94", {"start": v(0, -104.25) * mm, "end": v(0, -74.25) * mm, "construction": true});
            skSolve(sketch);
        }
        {
            var Q0;
            {var subQ0=sQuery(id+"F16.wireOp",EDGE,"E80");Q0=makeQuery(id+"F16.imprint","IMPRINT",FACE,{"disambiguationData":[TD([[makeQuery(id+"F16.imprint","IMPRINT",EDGE,{"derivedFrom":subQ0}),-1.0]])]});}
            var Q1;
            {var subQ0=sQuery(id+"F16.wireOp",EDGE,"E88.MirrorCS");Q1=makeQuery(id+"F16.imprint","IMPRINT",FACE,{"disambiguationData":[TD([[makeQuery(id+"F16.imprint","IMPRINT",EDGE,{"derivedFrom":subQ0}),1.0]])]});}
            var Q2;
            Q2=makeQuery(id+"F2.opExtrude","CAP_FACE",FACE,{"disambiguationData":[OSD([sQuery(id+"F0.wireOp",EDGE,"E12"),sQuery(id+"F0.wireOp",EDGE,"E13"),sQuery(id+"F0.wireOp",EDGE,"E14"),sQuery(id+"F0.wireOp",EDGE,"E15"),sQuery(id+"F0.wireOp",EDGE,"E17.filletArc"),sQuery(id+"F0.wireOp",EDGE,"E18.filletArc"),sQuery(id+"F0.wireOp",EDGE,"E19.filletArc"),sQuery(id+"F0.wireOp",EDGE,"E20.filletArc"),sQuery(id+"F0.wireOp",EDGE,"E25.0"),sQuery(id+"F0.wireOp",EDGE,"E25.1"),sQuery(id+"F0.wireOp",EDGE,"E25.2"),sQuery(id+"F0.wireOp",EDGE,"E25.3"),sQuery(id+"F0.wireOp",EDGE,"E25.4"),sQuery(id+"F0.wireOp",EDGE,"E25.5"),sQuery(id+"F0.wireOp",EDGE,"E25.6"),sQuery(id+"F0.wireOp",EDGE,"E25.7")])],"isStart":false});
            extrude(context, id + "F17", {"entities" : qUnion([Q0, Q1]), "endBound" : BoundingType.UP_TO_SURFACE, "endBoundEntityFace" : qUnion([Q2]), "depth" : 25 * mm});
        }
    });
